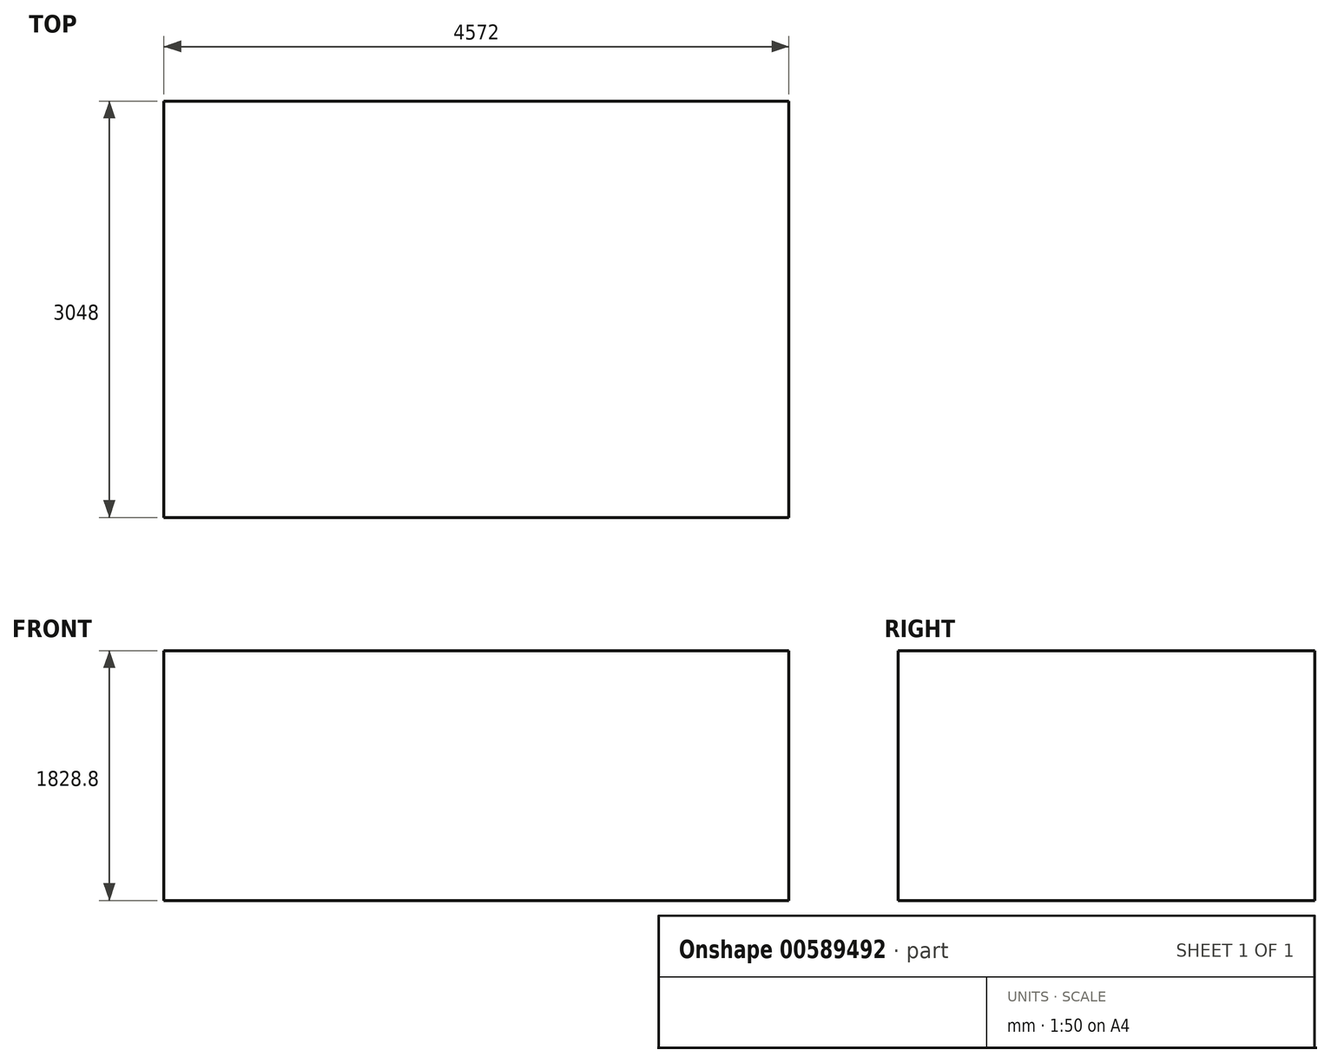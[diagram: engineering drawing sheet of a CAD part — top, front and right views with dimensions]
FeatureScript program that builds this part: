
annotation { "Feature Type Name" : "Feature", "Feature Type Description" : "" }
export const myFeature = defineFeature(function(context is Context, id is Id, definition is map)
    precondition{}
    {
        {
            var Q0;
            Q0=qCreatedBy(makeId("Top.planeOp"),FACE);
            var sketch = newSketch(context, id + "F0", { "sketchPlane" : qUnion([Q0])});
            skLineSegment(sketch, "E0.bottom", {"start": v(2286, -1524) * mm, "end": v(-2286, -1524) * mm});
            skLineSegment(sketch, "E0.top", {"start": v(2286, 1524) * mm, "end": v(-2286, 1524) * mm});
            skLineSegment(sketch, "E0.left", {"start": v(2286, -1524) * mm, "end": v(2286, 1524) * mm});
            skLineSegment(sketch, "E0.right", {"start": v(-2286, -1524) * mm, "end": v(-2286, 1524) * mm});
            skPoint(sketch, "E0.middle", {"position": v(0, 0) * mm});
            skSolve(sketch);
        }
        {
            var Q0;
            Q0=makeQuery(id+"F0.imprint","IMPRINT",FACE,{"disambiguationData":[TD([[makeQuery(id+"F0.imprint","IMPRINT",EDGE,{"derivedFrom":sQuery(id+"F0.wireOp",EDGE,"E0.bottom")}),-1.0]])]});
            extrude(context, id + "F1", {"entities" : qUnion([Q0]), "oppositeDirection" : true, "depth" : 1828.8 * mm, "offsetDistance" : 30.48 * mm});
        }
    });
